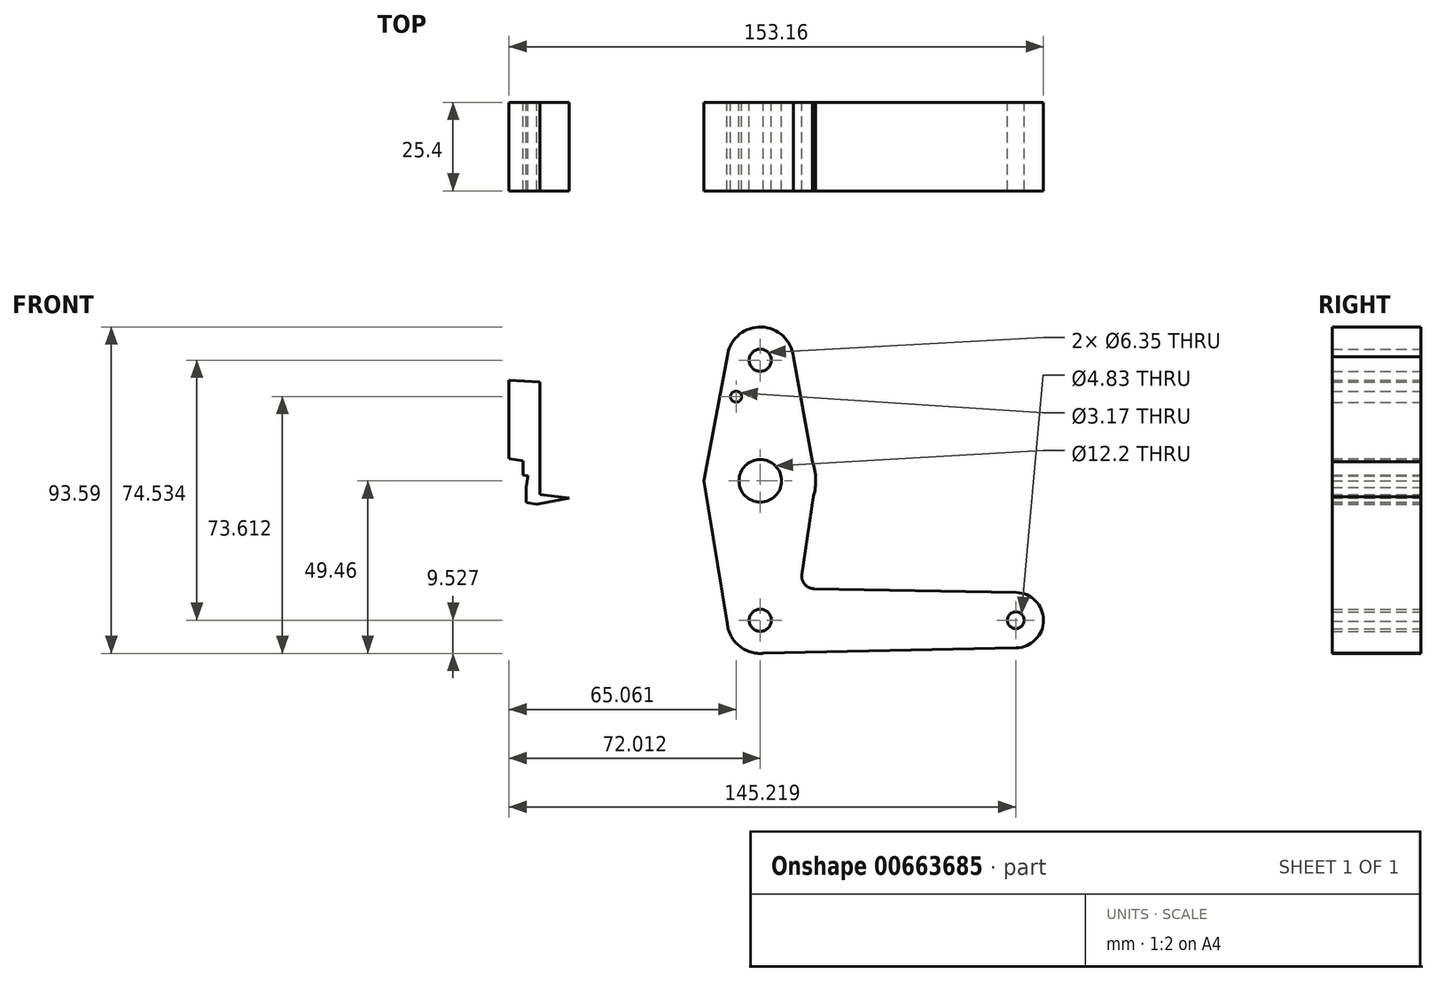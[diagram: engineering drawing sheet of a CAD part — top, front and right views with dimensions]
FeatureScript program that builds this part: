
annotation { "Feature Type Name" : "Feature", "Feature Type Description" : "" }
export const myFeature = defineFeature(function(context is Context, id is Id, definition is map)
    precondition{}
    {
        {
            var Q0;
            Q0=qCreatedBy(makeId("Front.planeOp"),FACE);
            var sketch = newSketch(context, id + "F0", { "sketchPlane" : qUnion([Q0])});
            skLineSegment(sketch, "E0", {"start": v(-48.75, 34.6) * mm, "end": v(-48.75, -39.93) * mm});
            skLineSegment(sketch, "E1", {"start": v(-48.75, -39.93) * mm, "end": v(0, -39.93) * mm});
            skLineSegment(sketch, "E2", {"start": v(24.46, -39.93) * mm, "end": v(0, -39.93) * mm});
            skCircle(sketch, "E3", {"center": v(-48.75, 34.6) * mm, "radius": 9.53 * mm});
            skCircle(sketch, "E4", {"center": v(-48.75, 0) * mm, "radius": 15.88 * mm});
            skCircle(sketch, "E5", {"center": v(-48.75, -39.93) * mm, "radius": 9.53 * mm});
            skCircle(sketch, "E6", {"center": v(24.46, -39.93) * mm, "radius": 7.94 * mm});
            skLineSegment(sketch, "E7", {"start": v(-58.1, 36.38) * mm, "end": v(-64.9, 0) * mm});
            skLineSegment(sketch, "E8", {"start": v(-64.9, 0) * mm, "end": v(-57.87, -42.68) * mm});
            skLineSegment(sketch, "E9", {"start": v(-32.87, 0) * mm, "end": v(-36.82, -26.92) * mm});
            skLineSegment(sketch, "E10", {"start": v(-33.44, -30.9) * mm, "end": v(24.63, -32) * mm});
            skLineSegment(sketch, "E11", {"start": v(-49.24, -49.45) * mm, "end": v(24.63, -47.87) * mm});
            skLineSegment(sketch, "E12", {"start": v(-39.27, 35.56) * mm, "end": v(-32.87, 0) * mm});
            skLineSegment(sketch, "E13", {"start": v(-111.92, -3.88) * mm, "end": v(-111.92, 28.34) * mm});
            skLineSegment(sketch, "E14", {"start": v(-111.92, 28.34) * mm, "end": v(-120.76, 28.8) * mm});
            skLineSegment(sketch, "E15", {"start": v(-120.76, 28.8) * mm, "end": v(-120.76, 6.36) * mm});
            skLineSegment(sketch, "E16", {"start": v(-120.76, 6.36) * mm, "end": v(-116.77, 5.77) * mm});
            skLineSegment(sketch, "E17", {"start": v(-116.77, 5.77) * mm, "end": v(-116.77, 3.5) * mm});
            skLineSegment(sketch, "E18", {"start": v(-116.77, 3.5) * mm, "end": v(-116.77, 1.66) * mm});
            skLineSegment(sketch, "E19", {"start": v(-116.77, 1.66) * mm, "end": v(-115.36, 1.45) * mm});
            skLineSegment(sketch, "E20", {"start": v(-115.36, 1.45) * mm, "end": v(-115.98, -2.8) * mm});
            skLineSegment(sketch, "E21", {"start": v(-115.98, -2.8) * mm, "end": v(-115.83, -1.82) * mm});
            skLineSegment(sketch, "E22", {"start": v(-115.83, -1.82) * mm, "end": v(-115.83, -6.23) * mm});
            skLineSegment(sketch, "E23", {"start": v(-115.83, -6.23) * mm, "end": v(-112.75, -6.68) * mm});
            skLineSegment(sketch, "E24", {"start": v(-112.75, -6.68) * mm, "end": v(-103.53, -4.89) * mm});
            skLineSegment(sketch, "E25", {"start": v(-103.53, -4.89) * mm, "end": v(-111.92, -3.88) * mm});
            skCircle(sketch, "E26", {"center": v(-55.7, 24.15) * mm, "radius": 1.59 * mm});
            skCircle(sketch, "E27", {"center": v(-48.75, 34.6) * mm, "radius": 3.18 * mm});
            skCircle(sketch, "E28", {"center": v(-48.75, 0) * mm, "radius": 6.1 * mm});
            skCircle(sketch, "E29", {"center": v(-48.75, -39.93) * mm, "radius": 3.18 * mm});
            skCircle(sketch, "E30", {"center": v(24.46, -39.93) * mm, "radius": 2.41 * mm});
            skPoint(sketch, "E31.newPointB", {"position": v(-51.9, -30.56) * mm});
            skArc(sketch, "E31.filletArc", {"start": v(-36.82, -26.92) * mm, "mid": v(-36.03, -29.68) * mm, "end": v(-33.44, -30.9) * mm});
            skSolve(sketch);
        }
        {
            var Q0;
            Q0 = qSketchRegion(id + "F0", true);
            var Q1;
            {var subQ0=sQuery(id+"F0.wireOp",EDGE,"E5");var subQ1=sQuery(id+"F0.wireOp",EDGE,"E0");var subQ2=makeQuery(id+"F0.imprint","INTERSECT",VERTEX,{"derivedFrom":[subQ1,subQ0]});Q1=makeQuery(id+"F0.imprint","IMPRINT",FACE,{"disambiguationData":[TD([[makeQuery(id+"F0.imprint","IMPRINT",EDGE,{"disambiguationData":[TD([[subQ2,-1.0]])],"derivedFrom":subQ1}),1.0]])]});}
            extrude(context, id + "F1", {"entities" : qUnion([Q0, Q1]), "depth" : 25.4 * mm, "offsetDistance" : 25.4 * mm});
        }
    });
